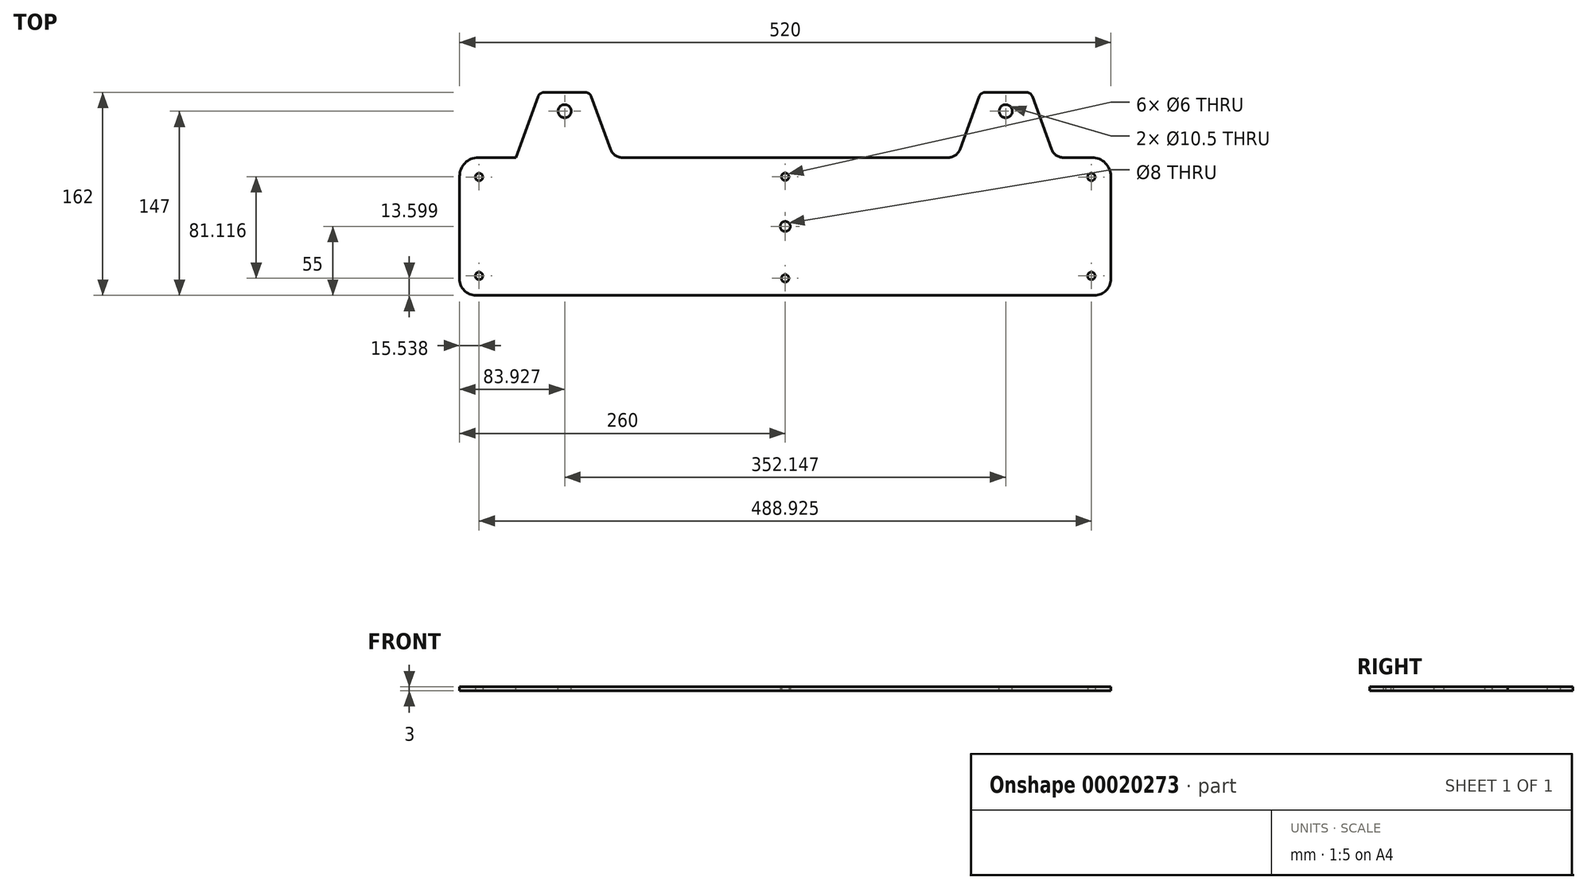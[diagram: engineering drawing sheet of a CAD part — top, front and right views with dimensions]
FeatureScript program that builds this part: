
annotation { "Feature Type Name" : "Feature", "Feature Type Description" : "" }
export const myFeature = defineFeature(function(context is Context, id is Id, definition is map)
    precondition{}
    {
        {
            var Q0;
            Q0=qCreatedBy(makeId("Top.planeOp"),FACE);
            var sketch = newSketch(context, id + "F0", { "sketchPlane" : qUnion([Q0])});
            skLineSegment(sketch, "E0.bottom", {"start": v(-245, 55) * mm, "end": v(245, 55) * mm});
            skLineSegment(sketch, "E0.top", {"start": v(-247, -55) * mm, "end": v(247, -55) * mm});
            skLineSegment(sketch, "E0.left", {"start": v(-260, 40) * mm, "end": v(-260, -42) * mm});
            skLineSegment(sketch, "E0.right", {"start": v(260, 40) * mm, "end": v(260, -42) * mm});
            skLineSegment(sketch, "E1", {"start": v(0, 55) * mm, "end": v(0, 0) * mm, "construction": true});
            skLineSegment(sketch, "E2", {"start": v(0, 0) * mm, "end": v(-260, 0) * mm, "construction": true});
            skPoint(sketch, "E3.visualSharp", {"position": v(-260, 55) * mm});
            skArc(sketch, "E3.filletArc", {"start": v(-260, 55) * mm, "mid": v(-260, 55) * mm, "end": v(-260, 55) * mm});
            skPoint(sketch, "E4.visualSharp", {"position": v(-260, -55) * mm});
            skArc(sketch, "E4.filletArc", {"start": v(-260, -42) * mm, "mid": v(-256.2, -51.2) * mm, "end": v(-247, -55) * mm});
            skPoint(sketch, "E5.visualSharp", {"position": v(260, -55) * mm});
            skArc(sketch, "E5.filletArc", {"start": v(247, -55) * mm, "mid": v(256.2, -51.2) * mm, "end": v(260, -42) * mm});
            skCircle(sketch, "E6", {"center": v(0, 0) * mm, "radius": 4 * mm});
            skCircle(sketch, "E7", {"center": v(0, 39.71) * mm, "radius": 3 * mm});
            skCircle(sketch, "E8", {"center": v(0, -41.4) * mm, "radius": 3 * mm});
            skCircle(sketch, "E9", {"center": v(-244.46, 39.46) * mm, "radius": 3 * mm});
            skCircle(sketch, "E10", {"center": v(-244.46, -39.46) * mm, "radius": 3 * mm});
            skCircle(sketch, "E11", {"center": v(244.46, -39.46) * mm, "radius": 3 * mm});
            skCircle(sketch, "E12", {"center": v(244.46, 39.46) * mm, "radius": 3 * mm});
            skLineSegment(sketch, "E13.left", {"start": v(0, 8.6) * mm, "end": v(0, 8.6) * mm});
            skLineSegment(sketch, "E13.right", {"start": v(157.87, 8.6) * mm, "end": v(157.87, 8.6) * mm});
            skLineSegment(sketch, "E14.0", {"start": v(220, 55) * mm, "end": v(220, 105) * mm});
            skLineSegment(sketch, "E15.0", {"start": v(-220, 55) * mm, "end": v(-220, 105) * mm});
            skArc(sketch, "E16.filletArc", {"start": v(-245, 55) * mm, "mid": v(-255.6, 50.6) * mm, "end": v(-260, 40) * mm});
            skPoint(sketch, "E17.visualSharp", {"position": v(260, 55) * mm});
            skArc(sketch, "E17.filletArc", {"start": v(260, 40) * mm, "mid": v(255.6, 50.6) * mm, "end": v(245, 55) * mm});
            skSolve(sketch);
        }
        {
            var Q0;
            Q0=makeQuery(id+"F0.imprint","IMPRINT",FACE,{"disambiguationData":[TD([[makeQuery(id+"F0.imprint","IMPRINT",EDGE,{"derivedFrom":sQuery(id+"F0.wireOp",EDGE,"E0.top")}),1.0]])]});
            extrude(context, id + "F1", {"entities" : qUnion([Q0]), "depth" : 3 * mm});
        }
        {
            var Q0;
            Q0=makeQuery(id+"F1.opExtrude","CAP_FACE",FACE,{"disambiguationData":[OSD([sQuery(id+"F0.wireOp",EDGE,"E0.bottom"),sQuery(id+"F0.wireOp",EDGE,"E0.top"),sQuery(id+"F0.wireOp",EDGE,"E0.left"),sQuery(id+"F0.wireOp",EDGE,"E0.right"),sQuery(id+"F0.wireOp",EDGE,"E3.filletArc"),sQuery(id+"F0.wireOp",EDGE,"E4.filletArc"),sQuery(id+"F0.wireOp",EDGE,"E5.filletArc"),sQuery(id+"F0.wireOp",EDGE,"E6"),sQuery(id+"F0.wireOp",EDGE,"E7"),sQuery(id+"F0.wireOp",EDGE,"E8"),sQuery(id+"F0.wireOp",EDGE,"E9"),sQuery(id+"F0.wireOp",EDGE,"E10"),sQuery(id+"F0.wireOp",EDGE,"E11"),sQuery(id+"F0.wireOp",EDGE,"E12")])],"isStart":false});
            var sketch = newSketch(context, id + "F2", { "sketchPlane" : qUnion([Q0])});
            skLineSegment(sketch, "E18", {"start": v(-192.57, 107) * mm, "end": v(-159.57, 107) * mm});
            skLineSegment(sketch, "E19", {"start": v(-154.88, 103.71) * mm, "end": v(-137.15, 55) * mm});
            skLineSegment(sketch, "E20", {"start": v(-197.27, 103.71) * mm, "end": v(-215, 55) * mm});
            skLineSegment(sketch, "E21", {"start": v(-215, 55) * mm, "end": v(-137.15, 55) * mm});
            skPoint(sketch, "E22.visualSharp", {"position": v(-196.07, 107) * mm});
            skArc(sketch, "E22.filletArc", {"start": v(-192.57, 107) * mm, "mid": v(-195.44, 106.1) * mm, "end": v(-197.27, 103.71) * mm});
            skPoint(sketch, "E23.visualSharp", {"position": v(-156.07, 107) * mm});
            skArc(sketch, "E24.filletArc", {"start": v(-154.88, 103.71) * mm, "mid": v(-156.7, 106.1) * mm, "end": v(-159.57, 107) * mm});
            skLineSegment(sketch, "E25", {"start": v(-176.07, 107) * mm, "end": v(-176.07, 92) * mm, "construction": true});
            skCircle(sketch, "E26", {"center": v(-176.07, 92) * mm, "radius": 5.25 * mm});
            skSolve(sketch);
        }
        {
            var Q0;
            Q0 = qSketchRegion(id + "F2", true);
            extrude(context, id + "F3", {"entities" : qUnion([Q0]), "oppositeDirection" : true, "depth" : 3 * mm});
        }
        {
            var Q0;
            Q0=makeQuery(id+"F3.opExtrude","SWEPT_BODY",BODY,{"disambiguationData":[OSD([sQuery(id+"F2.wireOp",EDGE,"E18"),sQuery(id+"F2.wireOp",EDGE,"E19"),sQuery(id+"F2.wireOp",EDGE,"E20"),sQuery(id+"F2.wireOp",EDGE,"E21"),sQuery(id+"F2.wireOp",EDGE,"E22.filletArc"),sQuery(id+"F2.wireOp",EDGE,"E24.filletArc"),sQuery(id+"F2.wireOp",EDGE,"E26")])]});
            var Q1;
            Q1=qCreatedBy(makeId("Right.planeOp"),FACE);
            mirror(context, id + "F4", {"operationType" : NewBodyOperationType.ADD, "entities" : qUnion([Q0]), "mirrorPlane" : qUnion([Q1])});
        }
        {
            var Q0;
            Q0=makeQuery(id+"F4.opPattern","COPY",EDGE,{"derivedFrom":makeQuery(id+"F3.opExtrude","SWEPT_EDGE",EDGE,{"disambiguationData":[OSD([sQuery(id+"F0.wireOp",EDGE,"E0.bottom"),sQuery(id+"F2.wireOp",EDGE,"E20"),sQuery(id+"F2.wireOp",EDGE,"E21")])]}),"instanceName":"1"});
            var Q1;
            Q1=makeQuery(id+"F4.opPattern","COPY",EDGE,{"derivedFrom":makeQuery(id+"F3.opExtrude","SWEPT_EDGE",EDGE,{"disambiguationData":[OSD([sQuery(id+"F0.wireOp",EDGE,"E0.bottom"),sQuery(id+"F2.wireOp",EDGE,"E19"),sQuery(id+"F2.wireOp",EDGE,"E21")])]}),"instanceName":"1"});
            var Q2;
            Q2=makeQuery(id+"F3.opExtrude","SWEPT_EDGE",EDGE,{"disambiguationData":[OSD([sQuery(id+"F0.wireOp",EDGE,"E0.bottom"),sQuery(id+"F2.wireOp",EDGE,"E19"),sQuery(id+"F2.wireOp",EDGE,"E21")])]});
            var Q3;
            Q3=makeQuery(id+"F3.opExtrude","SWEPT_EDGE",EDGE,{"disambiguationData":[OSD([sQuery(id+"F0.wireOp",EDGE,"E0.bottom"),sQuery(id+"F2.wireOp",EDGE,"E20"),sQuery(id+"F2.wireOp",EDGE,"E21")])]});
            fillet(context, id + "F5", {"entities" : qUnion([Q0, Q1, Q2, Q3]), "radius" : 10 * mm, "tangentPropagation" : true, "allowEdgeOverflow" : false});
        }
    });
